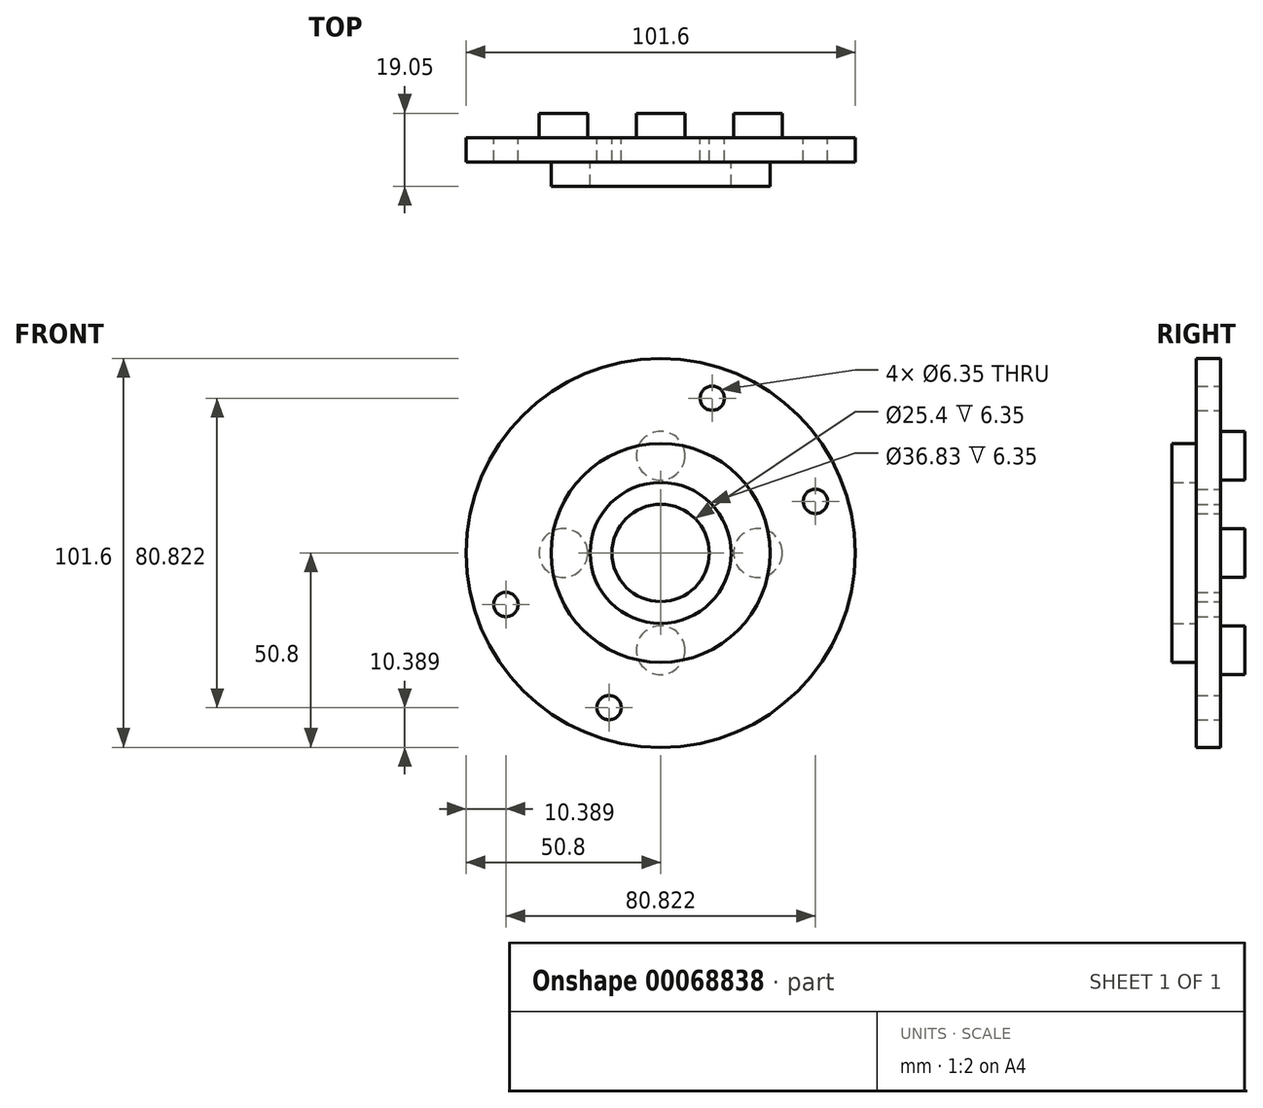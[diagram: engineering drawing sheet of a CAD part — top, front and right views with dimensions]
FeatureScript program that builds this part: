
annotation { "Feature Type Name" : "Feature", "Feature Type Description" : "" }
export const myFeature = defineFeature(function(context is Context, id is Id, definition is map)
    precondition{}
    {
        {
            var Q0;
            Q0=qCreatedBy(makeId("Front.planeOp"),FACE);
            var sketch = newSketch(context, id + "F0", { "sketchPlane" : qUnion([Q0])});
            skCircle(sketch, "E0", {"center": v(0, 0) * mm, "radius": 50.8 * mm});
            skCircle(sketch, "E1", {"center": v(0, 0) * mm, "radius": 12.7 * mm});
            skSolve(sketch);
        }
        {
            var Q0;
            Q0=makeQuery(id+"F0.imprint","IMPRINT",FACE,{"disambiguationData":[TD([[makeQuery(id+"F0.imprint","IMPRINT",EDGE,{"derivedFrom":sQuery(id+"F0.wireOp",EDGE,"E0")}),1.0]])]});
            extrude(context, id + "F1", {"entities" : qUnion([Q0]), "depth" : 6.35 * mm});
        }
        {
            var Q0;
            Q0=makeQuery(id+"F1.opExtrude","CAP_FACE",FACE,{"disambiguationData":[OSD([sQuery(id+"F0.wireOp",EDGE,"E0"),sQuery(id+"F0.wireOp",EDGE,"E1")])],"isStart":false});
            var sketch = newSketch(context, id + "F2", { "sketchPlane" : qUnion([Q0])});
            skCircle(sketch, "E2", {"center": v(0, 0) * mm, "radius": 18.41 * mm});
            skCircle(sketch, "E3", {"center": v(0, 0) * mm, "radius": 28.58 * mm});
            skSolve(sketch);
        }
        {
            var Q0;
            Q0=makeQuery(id+"F2.imprint","IMPRINT",FACE,{"disambiguationData":[TD([[makeQuery(id+"F2.imprint","IMPRINT",EDGE,{"derivedFrom":sQuery(id+"F2.wireOp",EDGE,"E2")}),-1.0]])]});
            extrude(context, id + "F3", {"entities" : qUnion([Q0]), "operationType" : NewBodyOperationType.ADD, "depth" : 6.35 * mm});
        }
        {
            var Q0;
            Q0=makeQuery(id+"F1.opExtrude","CAP_FACE",FACE,{"disambiguationData":[OSD([sQuery(id+"F0.wireOp",EDGE,"E0"),sQuery(id+"F0.wireOp",EDGE,"E1")])],"isStart":true});
            var sketch = newSketch(context, id + "F4", { "sketchPlane" : qUnion([Q0])});
            skCircle(sketch, "E4", {"center": v(0, 25.4) * mm, "radius": 6.35 * mm});
            skCircle(sketch, "E5", {"center": v(25.4, 0) * mm, "radius": 6.35 * mm});
            skCircle(sketch, "E6", {"center": v(0, -25.4) * mm, "radius": 6.35 * mm});
            skCircle(sketch, "E7", {"center": v(-25.4, 0) * mm, "radius": 6.35 * mm});
            skCircle(sketch, "E8", {"center": v(0, 0) * mm, "radius": 25.4 * mm, "construction": true});
            skSolve(sketch);
        }
        {
            var Q0;
            Q0=makeQuery(id+"F4.imprint","IMPRINT",FACE,{"disambiguationData":[TD([[makeQuery(id+"F4.imprint","IMPRINT",EDGE,{"derivedFrom":sQuery(id+"F4.wireOp",EDGE,"E4")}),1.0]])]});
            var Q1;
            Q1=makeQuery(id+"F4.imprint","IMPRINT",FACE,{"disambiguationData":[TD([[makeQuery(id+"F4.imprint","IMPRINT",EDGE,{"derivedFrom":sQuery(id+"F4.wireOp",EDGE,"E5")}),1.0]])]});
            var Q2;
            Q2=makeQuery(id+"F4.imprint","IMPRINT",FACE,{"disambiguationData":[TD([[makeQuery(id+"F4.imprint","IMPRINT",EDGE,{"derivedFrom":sQuery(id+"F4.wireOp",EDGE,"E6")}),1.0]])]});
            var Q3;
            Q3=makeQuery(id+"F4.imprint","IMPRINT",FACE,{"disambiguationData":[TD([[makeQuery(id+"F4.imprint","IMPRINT",EDGE,{"derivedFrom":sQuery(id+"F4.wireOp",EDGE,"E7")}),1.0]])]});
            extrude(context, id + "F5", {"entities" : qUnion([Q0, Q1, Q2, Q3]), "operationType" : NewBodyOperationType.ADD, "depth" : 6.35 * mm});
        }
        {
            var Q0;
            Q0=makeQuery(id+"F1.opExtrude","CAP_FACE",FACE,{"disambiguationData":[OSD([sQuery(id+"F0.wireOp",EDGE,"E0"),sQuery(id+"F0.wireOp",EDGE,"E1")])],"isStart":true});
            var sketch = newSketch(context, id + "F6", { "sketchPlane" : qUnion([Q0])});
            skCircle(sketch, "E9", {"center": v(-40.41, 13.47) * mm, "radius": 3.18 * mm});
            skCircle(sketch, "E10", {"center": v(13.47, -40.41) * mm, "radius": 3.18 * mm});
            skCircle(sketch, "E11", {"center": v(40.41, -13.47) * mm, "radius": 3.18 * mm});
            skCircle(sketch, "E12", {"center": v(-13.47, 40.41) * mm, "radius": 3.18 * mm});
            skLineSegment(sketch, "E13.bottom", {"start": v(13.47, -40.41) * mm, "end": v(40.41, -13.47) * mm, "construction": true});
            skLineSegment(sketch, "E13.top", {"start": v(-40.41, 13.47) * mm, "end": v(-13.47, 40.41) * mm, "construction": true});
            skLineSegment(sketch, "E13.left", {"start": v(13.47, -40.41) * mm, "end": v(-40.41, 13.47) * mm, "construction": true});
            skLineSegment(sketch, "E13.right", {"start": v(40.41, -13.47) * mm, "end": v(-13.47, 40.41) * mm, "construction": true});
            skLineSegment(sketch, "E14", {"start": v(0, -25.4) * mm, "end": v(-25.4, 0) * mm, "construction": true});
            skLineSegment(sketch, "E15", {"start": v(25.4, 0) * mm, "end": v(0, 25.4) * mm, "construction": true});
            skSolve(sketch);
        }
        {
            var Q0;
            Q0 = qSketchRegion(id + "F6", true);
            extrude(context, id + "F7", {"entities" : qUnion([Q0]), "operationType" : NewBodyOperationType.REMOVE, "oppositeDirection" : true, "depth" : 25.4 * mm});
        }
    });
